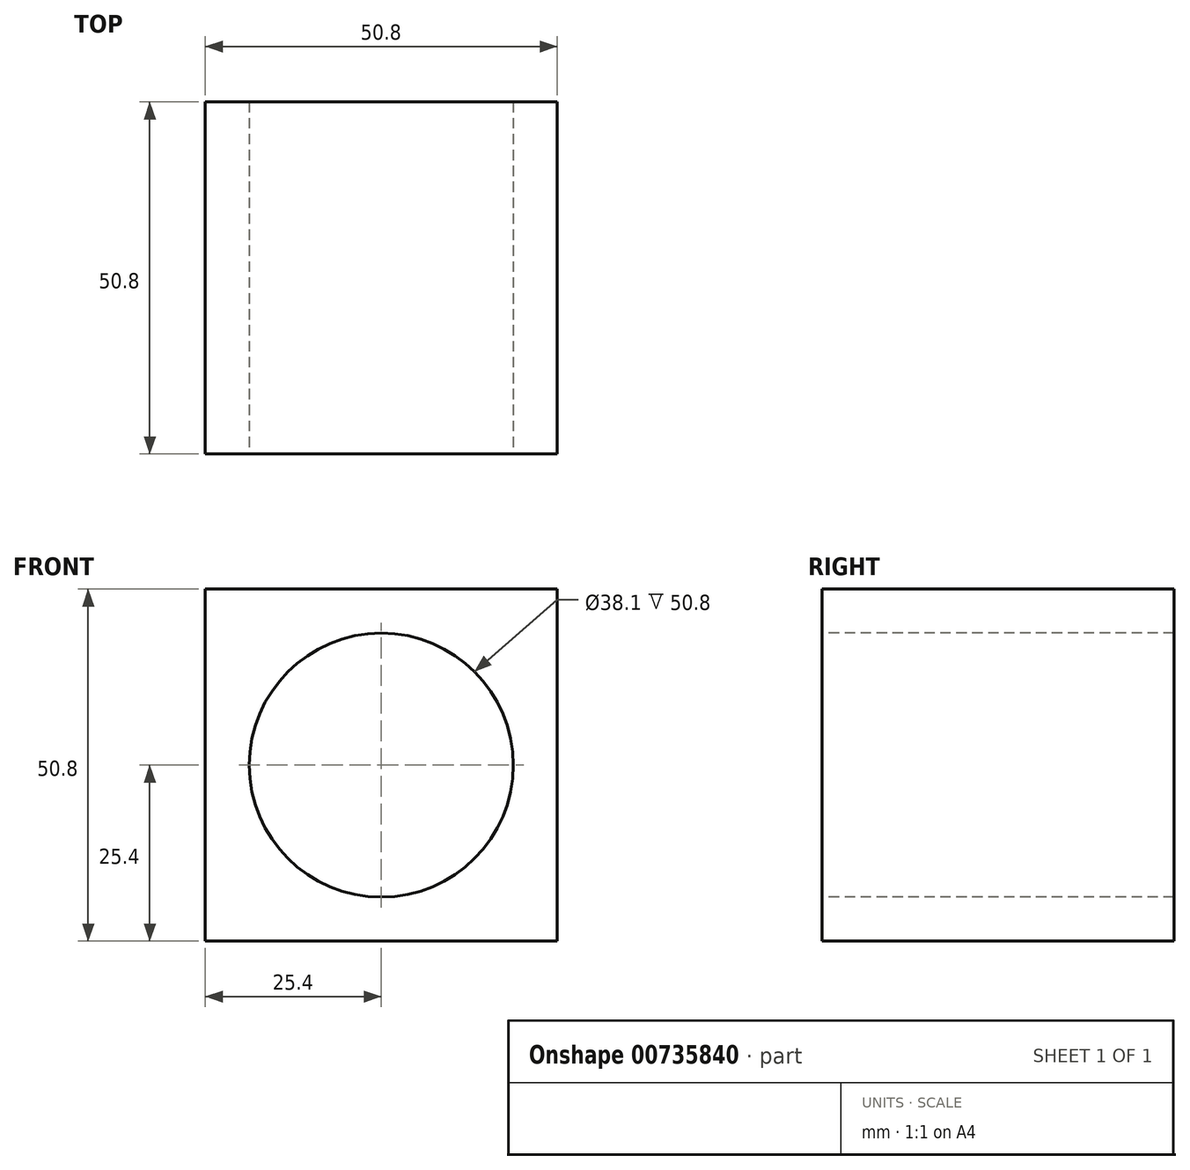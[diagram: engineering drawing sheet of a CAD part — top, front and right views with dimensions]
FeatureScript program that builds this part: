
annotation { "Feature Type Name" : "Feature", "Feature Type Description" : "" }
export const myFeature = defineFeature(function(context is Context, id is Id, definition is map)
    precondition{}
    {
        {
            var Q0;
            Q0=qCreatedBy(makeId("Front.planeOp"),FACE);
            var sketch = newSketch(context, id + "F0", { "sketchPlane" : qUnion([Q0])});
            skLineSegment(sketch, "E0", {"start": v(0, 0) * mm, "end": v(50.8, 0) * mm});
            skLineSegment(sketch, "E1", {"start": v(50.8, 0) * mm, "end": v(50.8, 50.8) * mm});
            skLineSegment(sketch, "E2", {"start": v(50.8, 50.8) * mm, "end": v(0, 50.8) * mm});
            skLineSegment(sketch, "E3", {"start": v(0, 50.8) * mm, "end": v(0, 0) * mm});
            skSolve(sketch);
        }
        {
            var Q0;
            Q0=makeQuery(id+"F0.imprint","IMPRINT",FACE,{"disambiguationData":[TD([[makeQuery(id+"F0.imprint","IMPRINT",EDGE,{"derivedFrom":sQuery(id+"F0.wireOp",EDGE,"E0")}),1.0]])]});
            extrude(context, id + "F1", {"entities" : qUnion([Q0]), "depth" : 50.8 * mm, "offsetDistance" : 25.4 * mm});
        }
        {
            var Q0;
            Q0=makeQuery(id+"F1.opExtrude","CAP_FACE",FACE,{"disambiguationData":[OSD([sQuery(id+"F0.wireOp",EDGE,"E0"),sQuery(id+"F0.wireOp",EDGE,"E1"),sQuery(id+"F0.wireOp",EDGE,"E2"),sQuery(id+"F0.wireOp",EDGE,"E3")])],"isStart":false});
            var sketch = newSketch(context, id + "F2", { "sketchPlane" : qUnion([Q0])});
            skCircle(sketch, "E4", {"center": v(24.03, 24.34) * mm, "radius": 15.76 * mm});
            skSolve(sketch);
        }
        {
            var Q0;
            Q0=makeQuery(id+"F2.imprint","IMPRINT",FACE,{"disambiguationData":[TD([[makeQuery(id+"F2.imprint","IMPRINT",EDGE,{"derivedFrom":sQuery(id+"F2.wireOp",EDGE,"E4")}),1.0]])]});
            extrude(context, id + "F3", {"entities" : qUnion([Q0]), "operationType" : NewBodyOperationType.REMOVE, "depth" : 50.8 * mm, "offsetDistance" : 25.4 * mm});
        }
        {
            var Q0;
            Q0=makeQuery(id+"F1.opExtrude","CAP_FACE",FACE,{"disambiguationData":[OSD([sQuery(id+"F0.wireOp",EDGE,"E0"),sQuery(id+"F0.wireOp",EDGE,"E1"),sQuery(id+"F0.wireOp",EDGE,"E2"),sQuery(id+"F0.wireOp",EDGE,"E3")])],"isStart":false});
            var sketch = newSketch(context, id + "F4", { "sketchPlane" : qUnion([Q0])});
            skCircle(sketch, "E5", {"center": v(25.4, 25.4) * mm, "radius": 19.05 * mm});
            skSolve(sketch);
        }
        {
            var Q0;
            Q0=makeQuery(id+"F4.imprint","IMPRINT",FACE,{"disambiguationData":[TD([[makeQuery(id+"F4.imprint","IMPRINT",EDGE,{"derivedFrom":sQuery(id+"F4.wireOp",EDGE,"E5")}),1.0]])]});
            extrude(context, id + "F5", {"entities" : qUnion([Q0]), "operationType" : NewBodyOperationType.REMOVE, "oppositeDirection" : true, "depth" : 50.8 * mm, "offsetDistance" : 25.4 * mm});
        }
    });
